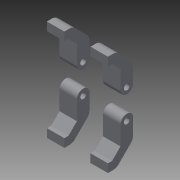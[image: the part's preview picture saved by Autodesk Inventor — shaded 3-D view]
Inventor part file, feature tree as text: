
AUTODESK INVENTOR PART (.ipt)
format: ipt  version: 2014 (Build 180170000, 170)  size: 151,552 bytes
history: native  units: in
note: dims shown in document units (in); Inventor stores cm internally (conversion verified against a paired STEP export)
features: extrude x4, sketch x4
ambient origin geometry x8: Origin, YZ Plane, XZ Plane, XY Plane, X Axis, Y Axis, Z Axis, Center Point
bodies: Solid1 (feature_tree)
feature tree (8):
  extrude  "Extrusion1"  Depth=15.748in TaperAngle=0.0deg
  extrude  "Extrusion6"  Depth=4.5in
  sketch  "Sketch7"  dims[d41=4.5in d42=6.4961in d43=0.0in]
  sketch  "Sketch8"  dims[d48=1.5in d49=1.5in d50=15.75in d51=0.0in d52=15.75in d53=0.0in]
  extrude  "Extrusion7"  Depth=6.4961in TaperAngle=0.0deg
  extrude  "Extrusion8"  Depth=1.5in
  sketch  "Sketch1"  dims[d8=45.0deg d24=15.748in d25=0.0in]
  sketch  "Sketch6"  dims[d39=4.5in d40=4.5in]
